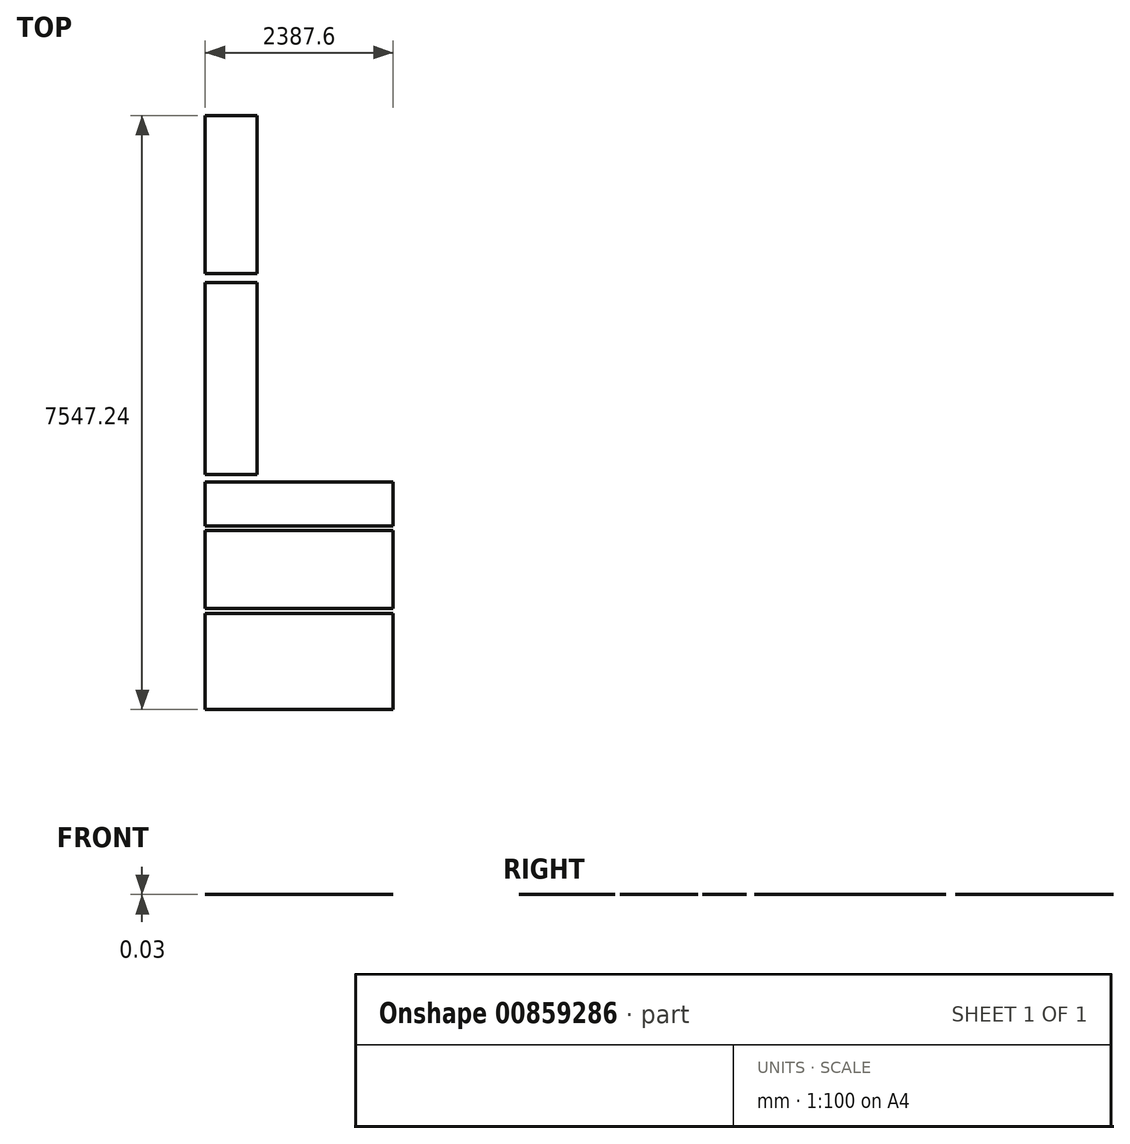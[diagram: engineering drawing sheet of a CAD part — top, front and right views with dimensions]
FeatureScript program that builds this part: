
annotation { "Feature Type Name" : "Feature", "Feature Type Description" : "" }
export const myFeature = defineFeature(function(context is Context, id is Id, definition is map)
    precondition{}
    {
        {
            var Q0;
            Q0=qCreatedBy(makeId("Top.planeOp"),FACE);
            var sketch = newSketch(context, id + "F0", { "sketchPlane" : qUnion([Q0])});
            skLineSegment(sketch, "E0.bottom", {"start": v(0, 0) * mm, "end": v(2387.6, 0) * mm});
            skLineSegment(sketch, "E0.top", {"start": v(0, 1219.2) * mm, "end": v(2387.6, 1219.2) * mm});
            skLineSegment(sketch, "E0.left", {"start": v(0, 0) * mm, "end": v(0, 1219.2) * mm});
            skLineSegment(sketch, "E0.right", {"start": v(2387.6, 0) * mm, "end": v(2387.6, 1219.2) * mm});
            skLineSegment(sketch, "E1.bottom", {"start": v(0, 1282.91) * mm, "end": v(2387.6, 1282.91) * mm});
            skLineSegment(sketch, "E1.top", {"start": v(0, 2273.51) * mm, "end": v(2387.6, 2273.51) * mm});
            skLineSegment(sketch, "E1.left", {"start": v(0, 1282.91) * mm, "end": v(0, 2273.51) * mm});
            skLineSegment(sketch, "E1.right", {"start": v(2387.6, 1282.91) * mm, "end": v(2387.6, 2273.51) * mm});
            skLineSegment(sketch, "E2.bottom", {"start": v(0, 2330.26) * mm, "end": v(2387.6, 2330.26) * mm});
            skLineSegment(sketch, "E2.top", {"start": v(0, 2889.06) * mm, "end": v(2387.6, 2889.06) * mm});
            skLineSegment(sketch, "E2.left", {"start": v(0, 2330.26) * mm, "end": v(0, 2889.06) * mm});
            skLineSegment(sketch, "E2.right", {"start": v(2387.6, 2330.26) * mm, "end": v(2387.6, 2889.06) * mm});
            skLineSegment(sketch, "E3.bottom", {"start": v(0, 2985.1) * mm, "end": v(660.4, 2985.1) * mm});
            skLineSegment(sketch, "E3.top", {"start": v(0, 5423.5) * mm, "end": v(660.4, 5423.5) * mm});
            skLineSegment(sketch, "E3.left", {"start": v(0, 2985.1) * mm, "end": v(0, 5423.5) * mm});
            skLineSegment(sketch, "E3.right", {"start": v(660.4, 2985.1) * mm, "end": v(660.4, 5423.5) * mm});
            skLineSegment(sketch, "E4.bottom", {"start": v(0, 5540.64) * mm, "end": v(660.4, 5540.64) * mm});
            skLineSegment(sketch, "E4.top", {"start": v(0, 7547.24) * mm, "end": v(660.4, 7547.24) * mm});
            skLineSegment(sketch, "E4.left", {"start": v(0, 5540.64) * mm, "end": v(0, 7547.24) * mm});
            skLineSegment(sketch, "E4.right", {"start": v(660.4, 5540.64) * mm, "end": v(660.4, 7547.24) * mm});
            skSolve(sketch);
        }
        {
            var Q0;
            Q0=makeQuery(id+"F0.imprint","IMPRINT",FACE,{"disambiguationData":[TD([[makeQuery(id+"F0.imprint","IMPRINT",EDGE,{"derivedFrom":sQuery(id+"F0.wireOp",EDGE,"E0.bottom")}),1.0]])]});
            var Q1;
            Q1=makeQuery(id+"F0.imprint","IMPRINT",FACE,{"disambiguationData":[TD([[makeQuery(id+"F0.imprint","IMPRINT",EDGE,{"derivedFrom":sQuery(id+"F0.wireOp",EDGE,"E2.bottom")}),1.0]])]});
            var Q2;
            Q2=makeQuery(id+"F0.imprint","IMPRINT",FACE,{"disambiguationData":[TD([[makeQuery(id+"F0.imprint","IMPRINT",EDGE,{"derivedFrom":sQuery(id+"F0.wireOp",EDGE,"E3.bottom")}),1.0]])]});
            var Q3;
            Q3=makeQuery(id+"F0.imprint","IMPRINT",FACE,{"disambiguationData":[TD([[makeQuery(id+"F0.imprint","IMPRINT",EDGE,{"derivedFrom":sQuery(id+"F0.wireOp",EDGE,"E4.bottom")}),1.0]])]});
            var Q4;
            Q4=makeQuery(id+"F0.imprint","IMPRINT",FACE,{"disambiguationData":[TD([[makeQuery(id+"F0.imprint","IMPRINT",EDGE,{"derivedFrom":sQuery(id+"F0.wireOp",EDGE,"E1.bottom")}),1.0]])]});
            extrude(context, id + "F1", {"entities" : qUnion([Q0, Q1, Q2, Q3, Q4]), "depth" : 3 / 101.6 * mm, "offsetDistance" : 25 * mm});
        }
    });
